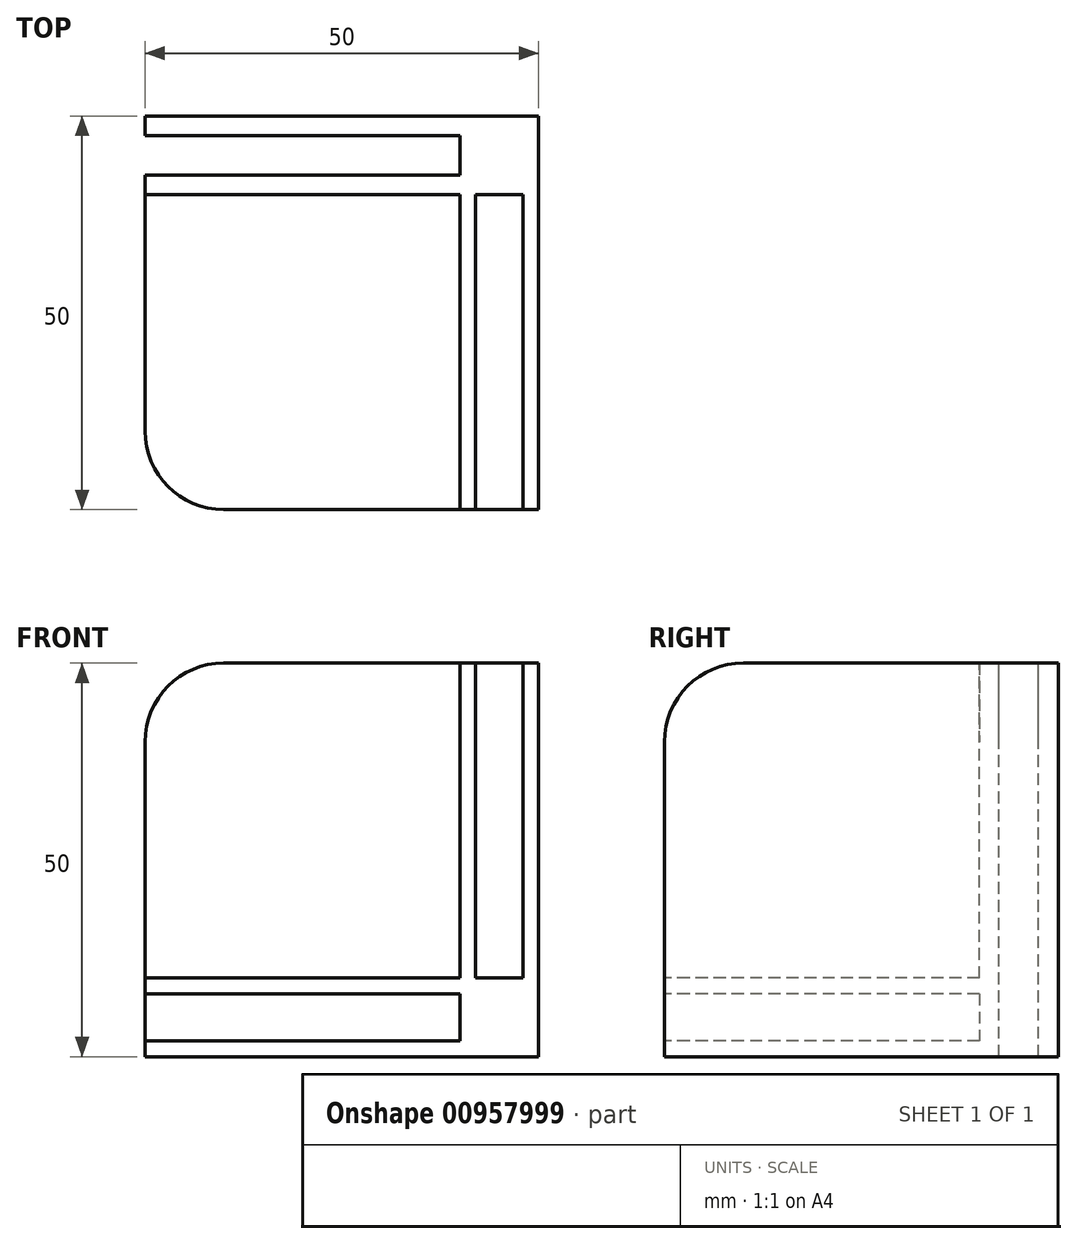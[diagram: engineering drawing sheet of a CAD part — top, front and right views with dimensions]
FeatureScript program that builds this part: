
annotation { "Feature Type Name" : "Feature", "Feature Type Description" : "" }
export const myFeature = defineFeature(function(context is Context, id is Id, definition is map)
    precondition{}
    {
        {
            var Q0;
            Q0=qCreatedBy(makeId("Top.planeOp"),FACE);
            var sketch = newSketch(context, id + "F0", { "sketchPlane" : qUnion([Q0])});
            skLineSegment(sketch, "E0.bottom", {"start": v(0, 0) * mm, "end": v(-50, 0) * mm});
            skLineSegment(sketch, "E0.top", {"start": v(0, -50) * mm, "end": v(-40, -50) * mm});
            skLineSegment(sketch, "E0.left", {"start": v(0, 0) * mm, "end": v(0, -50) * mm});
            skLineSegment(sketch, "E0.right", {"start": v(-50, 0) * mm, "end": v(-50, -40) * mm});
            skPoint(sketch, "E1.visualSharp", {"position": v(-50, -50) * mm});
            skArc(sketch, "E1.filletArc", {"start": v(-50, -40) * mm, "mid": v(-47.07, -47.07) * mm, "end": v(-40, -50) * mm});
            skSolve(sketch);
        }
        {
            var Q0;
            Q0=makeQuery(id+"F0.imprint","IMPRINT",FACE,{"disambiguationData":[TD([[makeQuery(id+"F0.imprint","IMPRINT",EDGE,{"derivedFrom":sQuery(id+"F0.wireOp",EDGE,"tNkWgY0K-5FoM-fzsk-HCrw-KOSka2LcS9h1.bottom")}),-1.0]])]});
            var Q1;
            Q1=makeQuery(id+"F0.imprint","IMPRINT",FACE,{"disambiguationData":[TD([[makeQuery(id+"F0.imprint","IMPRINT",EDGE,{"derivedFrom":sQuery(id+"F0.wireOp",EDGE,"E0.bottom")}),1.0]])]});
            var Q2;
            Q2=makeQuery(id+"F0.imprint","IMPRINT",FACE,{"disambiguationData":[TD([[makeQuery(id+"F0.imprint","IMPRINT",EDGE,{"derivedFrom":sQuery(id+"F0.wireOp",EDGE,"E0.top")}),-1.0]])]});
            var Q3;
            Q3=makeQuery(id+"F0.imprint","IMPRINT",FACE,{"disambiguationData":[TD([[makeQuery(id+"F0.imprint","IMPRINT",EDGE,{"derivedFrom":sQuery(id+"F0.wireOp",EDGE,"fvIwUqZD-S5C8-yHxi-N0ak-uGxWySerV2bo.bottom")}),1.0]])]});
            var Q4;
            Q4=makeQuery(id+"F0.imprint","IMPRINT",FACE,{"disambiguationData":[TD([[makeQuery(id+"F0.imprint","IMPRINT",EDGE,{"derivedFrom":sQuery(id+"F0.wireOp",EDGE,"JSCxDXyh-nDxv-V0qH-dKlW-7TGNpykFalIj.bottom")}),1.0]])]});
            extrude(context, id + "F1", {"entities" : qUnion([Q0, Q1, Q2, Q3, Q4]), "depth" : 10 * mm, "offsetDistance" : 25 * mm});
        }
        {
            var Q0;
            Q0=qCreatedBy(makeId("Right.planeOp"),FACE);
            var sketch = newSketch(context, id + "F2", { "sketchPlane" : qUnion([Q0])});
            skLineSegment(sketch, "E2.bottom", {"start": v(0, 10) * mm, "end": v(-50, 10) * mm});
            skLineSegment(sketch, "E2.top", {"start": v(0, 50) * mm, "end": v(-40, 50) * mm});
            skLineSegment(sketch, "E2.left", {"start": v(0, 10) * mm, "end": v(0, 50) * mm});
            skLineSegment(sketch, "E2.right", {"start": v(-50, 10) * mm, "end": v(-50, 40) * mm});
            skPoint(sketch, "E3.visualSharp", {"position": v(-50, 50) * mm});
            skArc(sketch, "E3.filletArc", {"start": v(-40, 50) * mm, "mid": v(-47.07, 47.07) * mm, "end": v(-50, 40) * mm});
            skSolve(sketch);
        }
        {
            var Q0;
            Q0=makeQuery(id+"F2.imprint","IMPRINT",FACE,{"disambiguationData":[TD([[makeQuery(id+"F2.imprint","IMPRINT",EDGE,{"derivedFrom":sQuery(id+"F2.wireOp",EDGE,"E2.bottom")}),-1.0]])]});
            extrude(context, id + "F3", {"entities" : qUnion([Q0]), "operationType" : NewBodyOperationType.ADD, "oppositeDirection" : true, "depth" : 10 * mm, "offsetDistance" : 25 * mm});
        }
        {
            var Q0;
            Q0=qCreatedBy(makeId("Front.planeOp"),FACE);
            var sketch = newSketch(context, id + "F4", { "sketchPlane" : qUnion([Q0])});
            skLineSegment(sketch, "E4.bottom", {"start": v(-10, 10) * mm, "end": v(-50, 10) * mm});
            skLineSegment(sketch, "E4.top", {"start": v(-10, 50) * mm, "end": v(-40, 50) * mm});
            skLineSegment(sketch, "E4.left", {"start": v(-10, 10) * mm, "end": v(-10, 50) * mm});
            skLineSegment(sketch, "E4.right", {"start": v(-50, 10) * mm, "end": v(-50, 40) * mm});
            skPoint(sketch, "E5.visualSharp", {"position": v(-50, 50) * mm});
            skArc(sketch, "E5.filletArc", {"start": v(-40, 50) * mm, "mid": v(-47.07, 47.07) * mm, "end": v(-50, 40) * mm});
            skSolve(sketch);
        }
        {
            var Q0;
            Q0=makeQuery(id+"F4.imprint","IMPRINT",FACE,{"disambiguationData":[TD([[makeQuery(id+"F4.imprint","IMPRINT",EDGE,{"derivedFrom":sQuery(id+"F4.wireOp",EDGE,"E4.bottom")}),-1.0]])]});
            extrude(context, id + "F5", {"entities" : qUnion([Q0]), "operationType" : NewBodyOperationType.ADD, "depth" : 10 * mm, "offsetDistance" : 25 * mm});
        }
        {
            var Q0;
            Q0=makeQuery(id+"F3.boolean.opBoolean","MERGE",FACE,{"derivedFrom":[makeQuery(id+"F1.opExtrude","SWEPT_FACE",FACE,{"disambiguationData":[OSD([sQuery(id+"F0.wireOp",EDGE,"E0.top")])]}),makeQuery(id+"F3.opExtrude","SWEPT_FACE",FACE,{"disambiguationData":[OSD([sQuery(id+"F2.wireOp",EDGE,"E2.right")])]})]});
            var sketch = newSketch(context, id + "F6", { "sketchPlane" : qUnion([Q0])});
            skLineSegment(sketch, "E6.bottom", {"start": v(-10, 2) * mm, "end": v(-60, 2) * mm});
            skLineSegment(sketch, "E6.top", {"start": v(-10, 8) * mm, "end": v(-60, 8) * mm});
            skLineSegment(sketch, "E6.left", {"start": v(-10, 2) * mm, "end": v(-10, 8) * mm});
            skLineSegment(sketch, "E6.right", {"start": v(-60, 2) * mm, "end": v(-60, 8) * mm});
            skLineSegment(sketch, "E7.bottom", {"start": v(-10, 2) * mm, "end": v(-15, 2) * mm});
            skLineSegment(sketch, "E7.top", {"start": v(-10, 52) * mm, "end": v(-15, 52) * mm});
            skLineSegment(sketch, "E8.bottom", {"start": v(-2, 10) * mm, "end": v(-8, 10) * mm});
            skLineSegment(sketch, "E8.top", {"start": v(-2, 60) * mm, "end": v(-8, 60) * mm});
            skLineSegment(sketch, "E8.left", {"start": v(-2, 10) * mm, "end": v(-2, 60) * mm});
            skLineSegment(sketch, "E8.right", {"start": v(-8, 10) * mm, "end": v(-8, 60) * mm});
            skSolve(sketch);
        }
        {
            var Q0;
            {var subQ0=sQuery(id+"F6.wireOp",EDGE,"E6.left");Q0=makeQuery(id+"F6.imprint","IMPRINT",FACE,{"disambiguationData":[TD([[makeQuery(id+"F6.imprint","IMPRINT",EDGE,{"derivedFrom":subQ0}),1.0]])]});}
            var Q1;
            {var subQ0=sQuery(id+"F6.wireOp",EDGE,"E6.right");Q1=makeQuery(id+"F6.imprint","IMPRINT",FACE,{"disambiguationData":[TD([[makeQuery(id+"F6.imprint","IMPRINT",EDGE,{"derivedFrom":subQ0}),-1.0]])]});}
            var Q2;
            {var subQ0=sQuery(id+"F6.wireOp",EDGE,"E6.right");Q2=makeQuery(id+"F6.imprint","IMPRINT",FACE,{"disambiguationData":[TD([[makeQuery(id+"F6.imprint","IMPRINT",EDGE,{"derivedFrom":subQ0}),-1.0]])]});}
            var Q3;
            {var subQ0=sQuery(id+"F6.wireOp",EDGE,"E8.bottom");Q3=makeQuery(id+"F6.imprint","IMPRINT",FACE,{"disambiguationData":[TD([[makeQuery(id+"F6.imprint","IMPRINT",EDGE,{"derivedFrom":subQ0}),-1.0]])]});}
            var Q4;
            {var subQ0=sQuery(id+"F6.wireOp",EDGE,"E8.top");Q4=makeQuery(id+"F6.imprint","IMPRINT",FACE,{"disambiguationData":[TD([[makeQuery(id+"F6.imprint","IMPRINT",EDGE,{"derivedFrom":subQ0}),1.0]])]});}
            extrude(context, id + "F7", {"entities" : qUnion([Q0, Q1, Q2, Q3, Q4]), "operationType" : NewBodyOperationType.REMOVE, "oppositeDirection" : true, "depth" : 40 * mm, "offsetDistance" : 25 * mm});
        }
        {
            var Q0;
            Q0=makeQuery(id+"F5.boolean.opBoolean","MERGE",FACE,{"derivedFrom":[makeQuery(id+"F3.opExtrude","SWEPT_FACE",FACE,{"disambiguationData":[OSD([sQuery(id+"F2.wireOp",EDGE,"E2.top")])]}),makeQuery(id+"F5.opExtrude","SWEPT_FACE",FACE,{"disambiguationData":[OSD([sQuery(id+"F4.wireOp",EDGE,"E4.top")])]})]});
            var sketch = newSketch(context, id + "F8", { "sketchPlane" : qUnion([Q0])});
            skLineSegment(sketch, "E9.bottom", {"start": v(-10, -2.5) * mm, "end": v(-60, -2.5) * mm});
            skLineSegment(sketch, "E9.top", {"start": v(-10, -7.5) * mm, "end": v(-60, -7.5) * mm});
            skLineSegment(sketch, "E9.left", {"start": v(-10, -2.5) * mm, "end": v(-10, -7.5) * mm});
            skLineSegment(sketch, "E9.right", {"start": v(-60, -2.5) * mm, "end": v(-60, -7.5) * mm});
            skSolve(sketch);
        }
        {
            var Q0;
            {var subQ0=sQuery(id+"F8.wireOp",EDGE,"E9.left");Q0=makeQuery(id+"F8.imprint","IMPRINT",FACE,{"disambiguationData":[TD([[makeQuery(id+"F8.imprint","IMPRINT",EDGE,{"derivedFrom":subQ0}),-1.0]])]});}
            var Q1;
            {var subQ0=sQuery(id+"F8.wireOp",EDGE,"E9.right");Q1=makeQuery(id+"F8.imprint","IMPRINT",FACE,{"disambiguationData":[TD([[makeQuery(id+"F8.imprint","IMPRINT",EDGE,{"derivedFrom":subQ0}),1.0]])]});}
            extrude(context, id + "F9", {"entities" : qUnion([Q0, Q1]), "operationType" : NewBodyOperationType.REMOVE, "endBound" : BoundingType.THROUGH_ALL, "oppositeDirection" : true, "depth" : 40 * mm, "offsetDistance" : 25 * mm});
        }
    });
